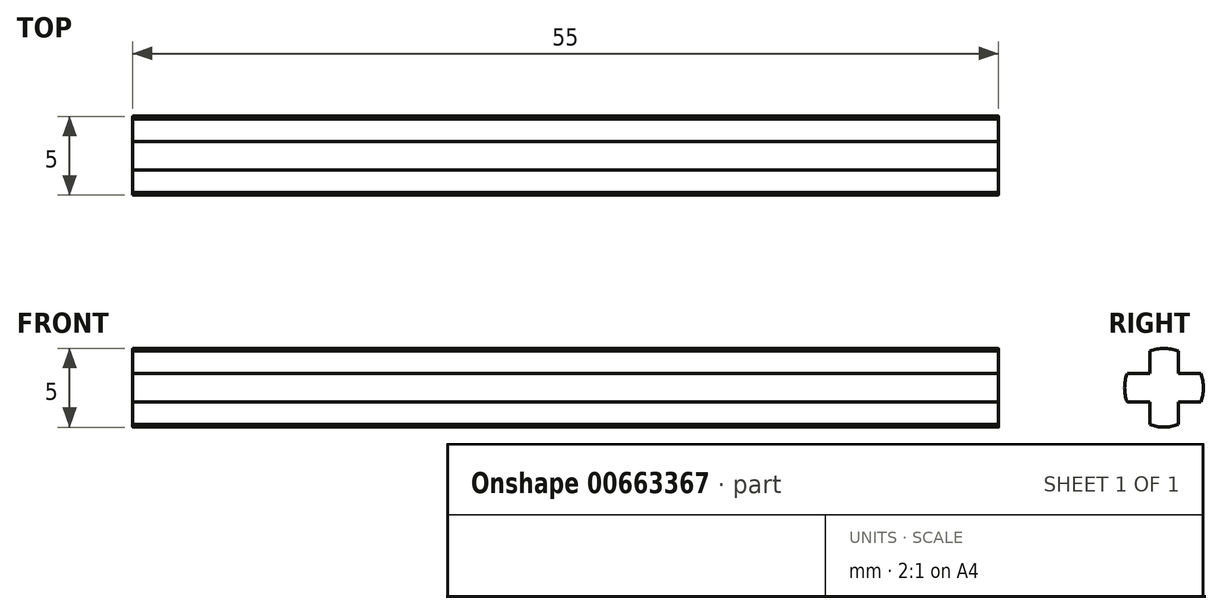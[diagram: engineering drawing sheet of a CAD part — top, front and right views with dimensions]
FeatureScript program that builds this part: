
annotation { "Feature Type Name" : "Feature", "Feature Type Description" : "" }
export const myFeature = defineFeature(function(context is Context, id is Id, definition is map)
    precondition{}
    {
        {
            var Q0;
            Q0=qCreatedBy(makeId("Right.planeOp"),FACE);
            var sketch = newSketch(context, id + "F0", { "sketchPlane" : qUnion([Q0])});
            skArc(sketch, "E0", {"start": v(2.4, -0.9) * mm, "mid": v(2.56, 0) * mm, "end": v(2.4, 0.9) * mm});
            skLineSegment(sketch, "E1.left", {"start": v(-0.84, 2.32) * mm, "end": v(-0.84, 0.9) * mm});
            skLineSegment(sketch, "E1.right", {"start": v(0.96, 2.32) * mm, "end": v(0.96, 0.9) * mm});
            skLineSegment(sketch, "E2.bottom", {"start": v(2.4, 0.9) * mm, "end": v(0.96, 0.9) * mm});
            skLineSegment(sketch, "E2.top", {"start": v(2.4, -0.9) * mm, "end": v(0.96, -0.9) * mm});
            skArc(sketch, "E3.trimOffspring", {"start": v(0.96, 2.32) * mm, "mid": v(0.06, 2.5) * mm, "end": v(-0.84, 2.32) * mm});
            skArc(sketch, "E4.trimOffspring", {"start": v(-2.27, 0.9) * mm, "mid": v(-2.44, 0) * mm, "end": v(-2.27, -0.9) * mm});
            skArc(sketch, "E5.trimOffspring", {"start": v(-0.84, -2.34) * mm, "mid": v(0.06, -2.5) * mm, "end": v(0.96, -2.34) * mm});
            skLineSegment(sketch, "E6.trimOffspring", {"start": v(-0.84, -0.9) * mm, "end": v(-0.84, -2.34) * mm});
            skLineSegment(sketch, "E7.trimOffspring", {"start": v(-0.84, 0.9) * mm, "end": v(-2.27, 0.9) * mm});
            skLineSegment(sketch, "E8.trimOffspring", {"start": v(0.96, -0.9) * mm, "end": v(0.96, -2.34) * mm});
            skLineSegment(sketch, "E9.trimOffspring", {"start": v(-0.84, -0.9) * mm, "end": v(-2.27, -0.9) * mm});
            skSolve(sketch);
        }
        {
            var Q0;
            Q0=qSketchRegion(id+"F0",true);
            extrude(context, id + "F1", {"entities" : qUnion([Q0]), "endBound" : BoundingType.SYMMETRIC, "depth" : 55 * mm, "offsetDistance" : 25 * mm});
        }
    });
